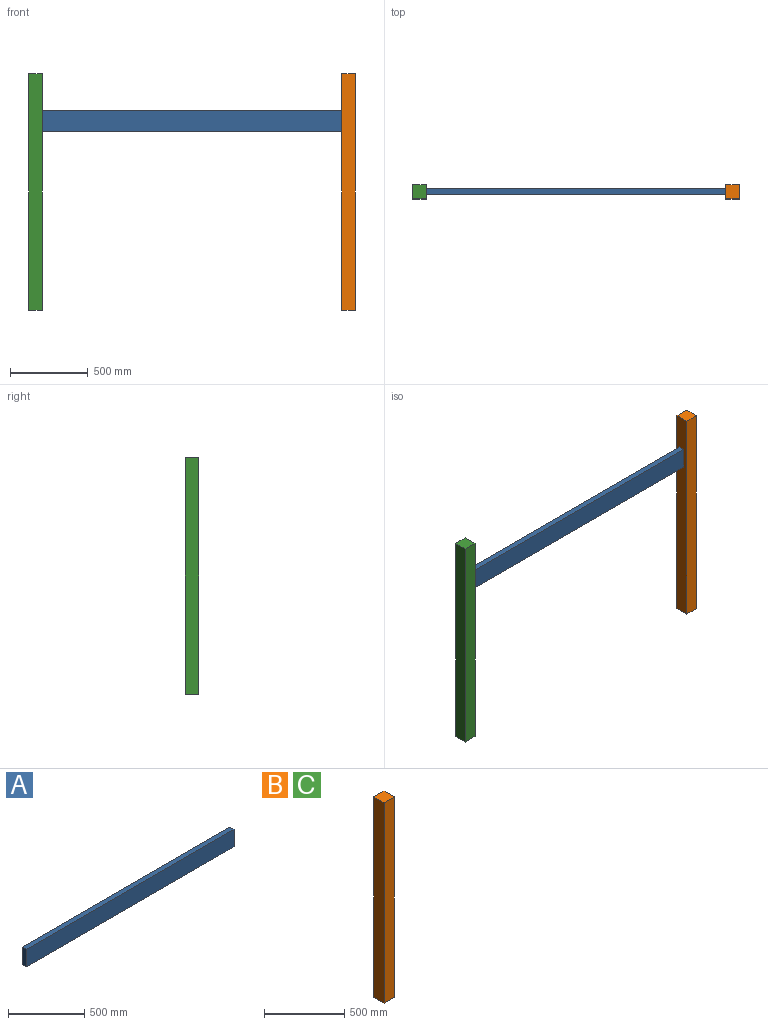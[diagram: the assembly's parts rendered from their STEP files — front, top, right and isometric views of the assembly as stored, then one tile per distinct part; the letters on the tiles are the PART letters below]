
ASSEMBLY  parts=3 mates=2
PART A: 6 faces, bbox 1930.4x38.1x139.7 mm
  f0: plane 1930.4x38.1mm, normal (0,0,1), area 73548.2mm2, adj f1,f3,f4,f5
  f1: plane 1930.4x139.7mm, normal (0,-1,0), area 269676.9mm2, adj f0,f2,f4,f5
  f2: plane 1930.4x38.1mm, normal (0,0,-1), area 73548.2mm2, adj f1,f3,f4,f5
  f3: plane 1930.4x139.7mm, normal (0,1,0), area 269676.9mm2, adj f0,f2,f4,f5
  f4: plane 139.7x38.1mm, normal (1,0,0), area 5322.6mm2, adj f0,f1,f2,f3
  f5: plane 139.7x38.1mm, normal (-1,0,0), area 5322.6mm2, adj f0,f1,f2,f3
PART B: 6 faces, bbox 88.9x88.9x1524 mm
  f0: plane 1524x88.9mm, normal (0,1,0), area 135483.6mm2, adj f1,f3,f4,f5
  f1: plane 1524x88.9mm, normal (-1,0,0), area 135483.6mm2, adj f0,f2,f4,f5
  f2: plane 1524x88.9mm, normal (0,-1,0), area 135483.6mm2, adj f1,f3,f4,f5
  f3: plane 1524x88.9mm, normal (1,0,0), area 135483.6mm2, adj f0,f2,f4,f5
  f4: plane 88.9x88.9mm, normal (0,0,1), area 7903.2mm2, adj f0,f1,f2,f3
  f5: plane 88.9x88.9mm, normal (0,0,-1), area 7903.2mm2, adj f0,f1,f2,f3
PART C: same geometry as B
PLACE A t=(-318.86,500.79,1484.12)mm
PLACE B t=(1680.79,465.96,310.52)mm
PLACE C rot(axis=(1,0,0),180deg) t=(-338.51,541.98,1834.52)mm
MATE fastened A.f4 <-> B.f1  axis (1,0,0) through (1611.54,503.97,1529.72)mm
MATE fastened C.f3 <-> A.f5  axis (1,0,0) through (-318.86,503.97,1072.52)mm
